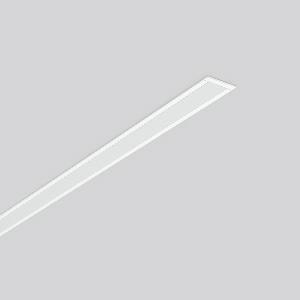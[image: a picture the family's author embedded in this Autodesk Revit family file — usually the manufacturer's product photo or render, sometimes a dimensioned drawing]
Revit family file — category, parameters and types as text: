
# Revit family: less_is_more_27_312178_002_1_6a55
name_source: partatom
category: Lighting Fixtures
units: mm (PartAtom-declared; Revit-internal decimal feet)

## family parameters
Cut with Voids When Loaded = No
Host = Face
Light Source = No
Part Type = Normal
Room Calculation Point = No
Round Connector Dimension = Use Diameter
Shared = No

## types (1)
- LESS IS MORE 27 (1 x LED Modul 840, 2900 lm, 4000)
    Apparent Load = 39 VA
    CIE Flux Codes = 48 79 96 100 100
    Color Rendering = 80
    Color Temperature = 4000
    Default Elevation = 1800 mm
    Description = Series: LESS IS MORE 27
Recessed ceiling and wall luminaire with slim design. Housing: extruded aluminium profile, powder-coated. End cap aluminium powder-coated. Diffuser made of non-yellowing plastic (PMMA), opal. Suitable for Recessed ceiling mounting, wall (recessed). External driver with connecting cable. 
Colour: traffic white, matt (RAL 9016)
Length: 1514 mm
Width: 38 mm
Height: 2 mm
Cut-out length: 1506 mm
Cut-out width: 30 mm
Recess height: 45-60 mm
Luminaire: recess height: 37 mm
Lamp: LED
Socket: without socket
Colour temperature: 4000K
Colour rendering index (CRI): 82
System power: 39 W
Rated luminous flux: 2900 lm
Luminous efficiency: 74 lm/W
Control gear: Regulated power supply
Protection class: II
Type of protection: IP 20
    Height = 0 mm  [stored 0 ft]
    Lamp = 1 x LED Modul 840
    Lamp Light Flux = 2900 lm
    Lamp count = 1
    Length = 1514 mm
    Lifetime = 50000 h
    Luminous efficacy = 74 lm/W
    Manufacturer = RZB
    ModVariant = No
    Model = 312178.002.1
    Mounting Place = Ceiling, Wall
    Mounting Type = Recessed
    Number of Poles = 1
    OnlyDefault = Yes
    Power Factor = 1
    Product Name = LESS IS MORE 27
    Product group = Recessed LED linear luminaires
    ProductGroupID = 407
    Protection Class = Protection class II
    Protection Degree = IP 20
    RLX_Detail_Level = 1
    RLX_Emergency_Light_Flux = 0 lm
    RLX_Emergency_Type = 0
    RLX_Emergency_Type_DB = No
    RlxData = <blob elided: 21553 chars, md5=1665f539>
    Socket = socket
    Standby Power = 0 W
    System Light Flux = 2900 lm
    System Power = 39 W
    Type Comments = Product without accessories
    Type Image = 312176.002.jpg
    URL = http://relux.com
    VarID = ---
    Voltage = 230 V
    Voltage Range = 220-240 V
    Weight = 0.00 kg
    Width = 38 mm

note: [stored X ft] marks values corroborated as IEEE doubles in the binary element streams (Revit-internal decimal feet)

## geometry (parser evidence)
native form markers: Blend x4, Sweep x12
no freeform markers — native parametric forms only
